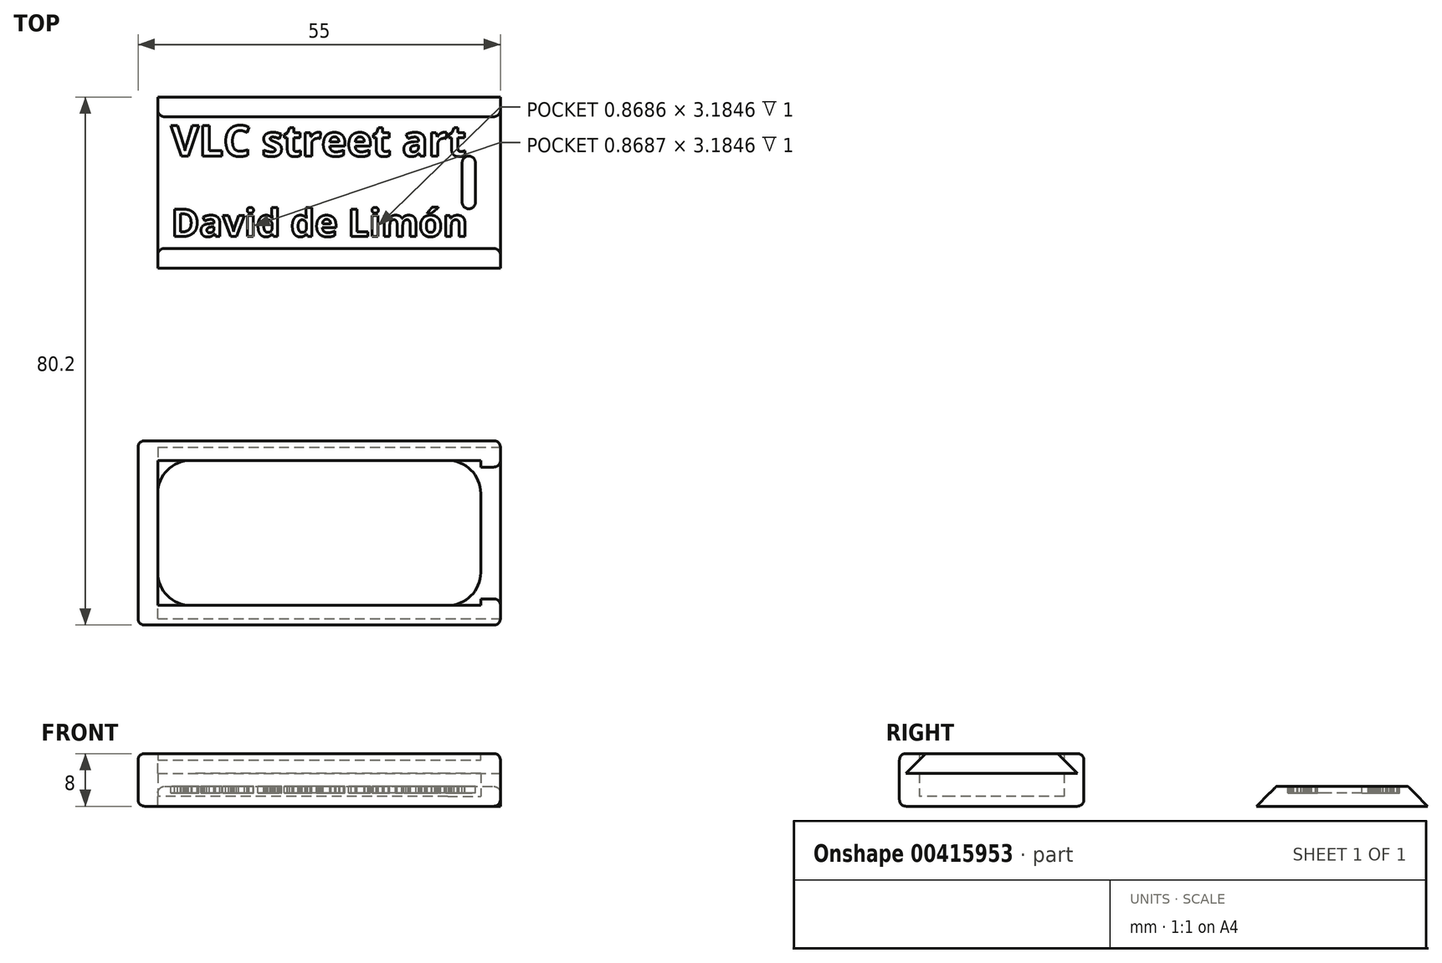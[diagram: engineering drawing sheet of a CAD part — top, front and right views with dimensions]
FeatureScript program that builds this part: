
annotation { "Feature Type Name" : "Feature", "Feature Type Description" : "" }
export const myFeature = defineFeature(function(context is Context, id is Id, definition is map)
    precondition{}
    {
        {
            assignVariable(context, id + "F0", {"name" : "Alto", "anyValue" : 2});
        }
        {
            assignVariable(context, id + "F1", {"name" : "largo", "anyValue" : 49});
        }
        {
            assignVariable(context, id + "F2", {"name" : "espesor", "anyValue" : 3});
        }
        {
            var Q0;
            Q0=qCreatedBy(makeId("Top.planeOp"),FACE);
            var sketch = newSketch(context, id + "F3", { "sketchPlane" : qUnion([Q0])});
            skLineSegment(sketch, "E0.bottom", {"start": v(24.5, 11) * mm, "end": v(-24.5, 11) * mm});
            skLineSegment(sketch, "E0.top", {"start": v(24.5, -11) * mm, "end": v(-24.5, -11) * mm});
            skLineSegment(sketch, "E0.left", {"start": v(24.5, 11) * mm, "end": v(24.5, -11) * mm});
            skLineSegment(sketch, "E0.right", {"start": v(-24.5, 11) * mm, "end": v(-24.5, -11) * mm});
            skPoint(sketch, "E0.middle", {"position": v(0, 0) * mm});
            skLineSegment(sketch, "E1.bottom", {"start": v(27.5, 14) * mm, "end": v(-27.5, 14) * mm});
            skLineSegment(sketch, "E1.top", {"start": v(27.5, -14) * mm, "end": v(-27.5, -14) * mm});
            skLineSegment(sketch, "E1.left", {"start": v(27.5, 14) * mm, "end": v(27.5, -14) * mm});
            skLineSegment(sketch, "E1.right", {"start": v(-27.5, 14) * mm, "end": v(-27.5, -14) * mm});
            skSolve(sketch);
        }
        {
            var Q0;
            Q0=makeQuery(id+"F3.imprint","IMPRINT",FACE,{"disambiguationData":[TD([[makeQuery(id+"F3.imprint","IMPRINT",EDGE,{"derivedFrom":sQuery(id+"F3.wireOp",EDGE,"E0.bottom")}),-1.0]])]});
            extrude(context, id + "F4", {"entities" : qUnion([Q0]), "depth" : (2 * getVariable(context, 'espesor') + getVariable(context, 'Alto')) * mm});
        }
        {
            var Q0;
            Q0=makeQuery(id+"F3.imprint","IMPRINT",FACE,{"disambiguationData":[TD([[makeQuery(id+"F3.imprint","IMPRINT",EDGE,{"derivedFrom":sQuery(id+"F3.wireOp",EDGE,"E0.bottom")}),1.0]])]});
            extrude(context, id + "F5", {"entities" : qUnion([Q0]), "operationType" : NewBodyOperationType.ADD, "depth" : (.5 * getVariable(context, 'espesor')) * mm});
        }
        {
            var Q0;
            Q0=makeQuery(id+"F4.opExtrude","SWEPT_FACE",FACE,{"disambiguationData":[OSD([sQuery(id+"F3.wireOp",EDGE,"E1.left")])]});
            var sketch = newSketch(context, id + "F6", { "sketchPlane" : qUnion([Q0])});
            skLineSegment(sketch, "E2", {"start": v(13, 5) * mm, "end": v(0, 5) * mm});
            skLineSegment(sketch, "E3", {"start": v(13, 5) * mm, "end": v(10, 8) * mm});
            skLineSegment(sketch, "E4", {"start": v(10, 8) * mm, "end": v(0, 8) * mm});
            skLineSegment(sketch, "E5.MirrorCS", {"start": v(-10, 8) * mm, "end": v(0, 8) * mm});
            skLineSegment(sketch, "E6.MirrorCS", {"start": v(-13, 5) * mm, "end": v(0, 5) * mm});
            skLineSegment(sketch, "E7.MirrorCS", {"start": v(-13, 5) * mm, "end": v(-10, 8) * mm});
            skSolve(sketch);
        }
        {
            var Q0;
            Q0=makeQuery(id+"F6.imprint","IMPRINT",FACE,{"disambiguationData":[TD([[makeQuery(id+"F6.imprint","IMPRINT",EDGE,{"derivedFrom":sQuery(id+"F6.wireOp",EDGE,"E2")}),-1.0]])]});
            extrude(context, id + "F7", {"entities" : qUnion([Q0]), "oppositeDirection" : true, "depth" : (getVariable(context, 'largo') + getVariable(context, 'espesor')) * mm});
        }
        {
            var Q0;
            Q0=makeQuery(id+"F7.opExtrude","SWEPT_BODY",BODY,{"disambiguationData":[OSD([sQuery(id+"F6.wireOp",EDGE,"SvTivXyg-bIk5-CTMK-920A-VDUx7YFhp4Xd"),sQuery(id+"F6.wireOp",EDGE,"NXYqkgHn-n5s3-E9hX-fx2y-YQDCVjQoqeno"),sQuery(id+"F6.wireOp",EDGE,"E2"),sQuery(id+"F6.wireOp",EDGE,"a3f9a05b-10ae-4f7d-80d1-88aed766babd0.MirrorCS"),sQuery(id+"F6.wireOp",EDGE,"1d98cbd7-637a-48a3-b701-6e80e332eecd0.MirrorCS"),sQuery(id+"F6.wireOp",EDGE,"f009dd86-6c0a-4020-9c2a-33f01825d16c0.MirrorCS")])]});
            transform(context, id + "F8", {"entities" : qUnion([Q0]), "transformType" : TransformType.TRANSLATION_3D, "dx" : 0 * mm, "dy" : 53.2 * mm, "dz" : 0 * mm, "makeCopy" : true});
        }
        {
            var Q0;
            Q0=makeQuery(id+"F4.opExtrude","SWEPT_EDGE",EDGE,{"disambiguationData":[OSD([sQuery(id+"F3.wireOp",EDGE,"E1.top"),sQuery(id+"F3.wireOp",EDGE,"E1.right")])]});
            var Q1;
            Q1=makeQuery(id+"F4.opExtrude","SWEPT_EDGE",EDGE,{"disambiguationData":[OSD([sQuery(id+"F3.wireOp",EDGE,"E1.bottom"),sQuery(id+"F3.wireOp",EDGE,"E1.right")])]});
            var Q2;
            Q2=makeQuery(id+"F4.opExtrude","SWEPT_EDGE",EDGE,{"disambiguationData":[OSD([sQuery(id+"F3.wireOp",EDGE,"E1.bottom"),sQuery(id+"F3.wireOp",EDGE,"E1.left")])]});
            var Q3;
            Q3=makeQuery(id+"F4.opExtrude","SWEPT_EDGE",EDGE,{"disambiguationData":[OSD([sQuery(id+"F3.wireOp",EDGE,"E1.top"),sQuery(id+"F3.wireOp",EDGE,"E1.left")])]});
            var Q4;
            Q4=makeQuery(id+"F4.opExtrude","CAP_EDGE",EDGE,{"disambiguationData":[OSD([sQuery(id+"F3.wireOp",EDGE,"E1.top")])],"isStart":false});
            var Q5;
            Q5=makeQuery(id+"F4.opExtrude","CAP_EDGE",EDGE,{"disambiguationData":[OSD([sQuery(id+"F3.wireOp",EDGE,"E1.bottom")])],"isStart":false});
            var Q6;
            Q6=makeQuery(id+"F4.opExtrude","CAP_EDGE",EDGE,{"disambiguationData":[OSD([sQuery(id+"F3.wireOp",EDGE,"E1.right")])],"isStart":false});
            var Q7;
            Q7=makeQuery(id+"F4.opExtrude","CAP_EDGE",EDGE,{"disambiguationData":[OSD([sQuery(id+"F3.wireOp",EDGE,"E1.top")])],"isStart":true});
            var Q8;
            Q8=makeQuery(id+"F4.opExtrude","CAP_EDGE",EDGE,{"disambiguationData":[OSD([sQuery(id+"F3.wireOp",EDGE,"E1.left")])],"isStart":true});
            var Q9;
            Q9=makeQuery(id+"F4.opExtrude","CAP_EDGE",EDGE,{"disambiguationData":[OSD([sQuery(id+"F3.wireOp",EDGE,"E1.bottom")])],"isStart":true});
            var Q10;
            Q10=makeQuery(id+"F4.opExtrude","CAP_EDGE",EDGE,{"disambiguationData":[OSD([sQuery(id+"F3.wireOp",EDGE,"E1.right")])],"isStart":true});
            var Q11;
            Q11=makeQuery(id+"F4.opExtrude","CAP_EDGE",EDGE,{"disambiguationData":[OSD([sQuery(id+"F3.wireOp",EDGE,"E1.left")])],"isStart":false});
            var Q12;
            Q12=makeQuery(id+"F8.opPattern","COPY",EDGE,{"derivedFrom":makeQuery(id+"F7.opExtrude","CAP_EDGE",EDGE,{"disambiguationData":[OSD([sQuery(id+"F6.wireOp",EDGE,"E4"),sQuery(id+"F6.wireOp",EDGE,"E5.MirrorCS")])],"isStart":false}),"instanceName":"1"});
            fillet(context, id + "F9", {"entities" : qUnion([Q0, Q1, Q2, Q3, Q4, Q5, Q6, Q7, Q8, Q9, Q10, Q11, Q12]), "radius" : 1 * mm, "tangentPropagation" : true, "allowEdgeOverflow" : false});
        }
        {
            var Q0;
            Q0=makeQuery(id+"F7.opExtrude","CAP_EDGE",EDGE,{"disambiguationData":[OSD([sQuery(id+"F6.wireOp",EDGE,"E4"),sQuery(id+"F6.wireOp",EDGE,"E5.MirrorCS")])],"isStart":true});
            var Q1;
            Q1=makeQuery(id+"F8.opPattern","COPY",EDGE,{"derivedFrom":makeQuery(id+"F7.opExtrude","CAP_EDGE",EDGE,{"disambiguationData":[OSD([sQuery(id+"F6.wireOp",EDGE,"E4"),sQuery(id+"F6.wireOp",EDGE,"E5.MirrorCS")])],"isStart":true}),"instanceName":"1"});
            fillet(context, id + "F10", {"entities" : qUnion([Q0, Q1]), "radius" : 1 * mm, "tangentPropagation" : true, "allowEdgeOverflow" : false});
        }
        {
            var Q0;
            Q0=makeQuery(id+"F7.opExtrude","SWEPT_BODY",BODY,{"disambiguationData":[OSD([sQuery(id+"F6.wireOp",EDGE,"E2"),sQuery(id+"F6.wireOp",EDGE,"E3"),sQuery(id+"F6.wireOp",EDGE,"E4"),sQuery(id+"F6.wireOp",EDGE,"E5.MirrorCS"),sQuery(id+"F6.wireOp",EDGE,"E6.MirrorCS"),sQuery(id+"F6.wireOp",EDGE,"E7.MirrorCS")])]});
            var Q1;
            Q1=makeQuery(id+"F4.opExtrude","SWEPT_BODY",BODY,{"disambiguationData":[OSD([sQuery(id+"F3.wireOp",EDGE,"E0.bottom"),sQuery(id+"F3.wireOp",EDGE,"E0.top"),sQuery(id+"F3.wireOp",EDGE,"E0.left"),sQuery(id+"F3.wireOp",EDGE,"E0.right"),sQuery(id+"F3.wireOp",EDGE,"E1.bottom"),sQuery(id+"F3.wireOp",EDGE,"E1.top"),sQuery(id+"F3.wireOp",EDGE,"E1.left"),sQuery(id+"F3.wireOp",EDGE,"E1.right")])]});
            booleanBodies(context, id + "F11", {"operationType" : BooleanOperationType.SUBTRACTION, "tools" : qUnion([Q0]), "targets" : qUnion([Q1])});
        }
        {
            var Q0;
            Q0=makeQuery(id+"F8.opPattern","COPY",FACE,{"derivedFrom":makeQuery(id+"F7.opExtrude","SWEPT_FACE",FACE,{"disambiguationData":[OSD([sQuery(id+"F6.wireOp",EDGE,"E4"),sQuery(id+"F6.wireOp",EDGE,"E5.MirrorCS")])]}),"instanceName":"1"});
            var sketch = newSketch(context, id + "F12", { "sketchPlane" : qUnion([Q0])});
            skText(sketch, "E8", { "text": "VLC street art", "fontName": "OpenSans-Bold.ttf"});
            skText(sketch, "E9", { "text": "David de Limón", "fontName": "OpenSans-Bold.ttf"});
            skLineSegment(sketch, "E10", {"start": v(-24.5, 53.2) * mm, "end": v(25.5, 53.2) * mm, "construction": true});
            skLineSegment(sketch, "E11", {"start": v(0, 35.02) * mm, "end": v(0, 65.75) * mm, "construction": true});
            skPoint(sketch, "E11.endSnap0", {"position": v(0, 59.55) * mm});
            skLineSegment(sketch, "E12.bottom", {"start": v(23.7, 56.2) * mm, "end": v(21.7, 56.2) * mm});
            skLineSegment(sketch, "E12.top", {"start": v(23.7, 50.2) * mm, "end": v(21.7, 50.2) * mm});
            skLineSegment(sketch, "E12.left", {"start": v(23.7, 56.2) * mm, "end": v(23.7, 50.2) * mm});
            skLineSegment(sketch, "E12.right", {"start": v(21.7, 56.2) * mm, "end": v(21.7, 50.2) * mm});
            skPoint(sketch, "E12.middle", {"position": v(22.7, 53.2) * mm});
            skArc(sketch, "E13", {"start": v(23.7, 56.2) * mm, "mid": v(22.7, 57.22) * mm, "end": v(21.7, 56.2) * mm});
            skArc(sketch, "E14", {"start": v(21.7, 50.2) * mm, "mid": v(22.7, 49.2) * mm, "end": v(23.7, 50.2) * mm});
            const initialGuessF12  = {"E8": [-0.0225, 0.0572, 1, 0, 0.0047], "E9": [-0.0225, 0.045, 1, 0, 0.0042]};
            skSetInitialGuess(sketch, initialGuessF12);
            skSolve(sketch);
        }
        {
            var Q0;
            Q0=qSketchRegion(id+"F12",true);
            extrude(context, id + "F13", {"entities" : qUnion([Q0]), "operationType" : NewBodyOperationType.REMOVE, "oppositeDirection" : true, "depth" : 1 * mm});
        }
        {
            var Q0;
            Q0=makeQuery(id+"F8.opPattern","COPY",BODY,{"derivedFrom":makeQuery(id+"F7.opExtrude","SWEPT_BODY",BODY,{"disambiguationData":[OSD([sQuery(id+"F6.wireOp",EDGE,"SvTivXyg-bIk5-CTMK-920A-VDUx7YFhp4Xd"),sQuery(id+"F6.wireOp",EDGE,"NXYqkgHn-n5s3-E9hX-fx2y-YQDCVjQoqeno"),sQuery(id+"F6.wireOp",EDGE,"E2"),sQuery(id+"F6.wireOp",EDGE,"a3f9a05b-10ae-4f7d-80d1-88aed766babd0.MirrorCS"),sQuery(id+"F6.wireOp",EDGE,"1d98cbd7-637a-48a3-b701-6e80e332eecd0.MirrorCS"),sQuery(id+"F6.wireOp",EDGE,"f009dd86-6c0a-4020-9c2a-33f01825d16c0.MirrorCS")])]}),"instanceName":"1"});
            transform(context, id + "F14", {"entities" : qUnion([Q0]), "transformType" : TransformType.TRANSLATION_3D, "dx" : 0 * mm, "dy" : 0 * mm, "dz" : -5 * mm, "makeCopy" : false});
        }
        {
            var Q0;
            {var subQ0=sQuery(id+"F6.wireOp",EDGE,"E6.MirrorCS");var subQ1=sQuery(id+"F6.wireOp",EDGE,"E2");var subQ2=sQuery(id+"F3.wireOp",EDGE,"E0.right");var subQ3=sQuery(id+"F3.wireOp",EDGE,"E0.top");Q0=makeQuery(id+"F11.opBoolean","SPLIT",EDGE,{"disambiguationData":[TD([makeQuery(id+"F7.opExtrude","SWEPT_FACE",FACE,{"disambiguationData":[OSD([subQ1,subQ0])]})])],"derivedFrom":makeQuery(id+"F4.opExtrude","SWEPT_EDGE",EDGE,{"disambiguationData":[OSD([subQ3,subQ2])]})});}
            var Q1;
            {var subQ0=sQuery(id+"F3.wireOp",EDGE,"E0.top");var subQ1=sQuery(id+"F3.wireOp",EDGE,"E0.left");Q1=makeQuery(id+"F11.opBoolean","SPLIT",EDGE,{"disambiguationData":[TD([makeQuery(id+"F7.opExtrude","SWEPT_FACE",FACE,{"disambiguationData":[OSD([sQuery(id+"F6.wireOp",EDGE,"E2"),sQuery(id+"F6.wireOp",EDGE,"E6.MirrorCS")])]})])],"derivedFrom":makeQuery(id+"F4.opExtrude","SWEPT_EDGE",EDGE,{"disambiguationData":[OSD([subQ0,subQ1])]})});}
            var Q2;
            {var subQ0=sQuery(id+"F3.wireOp",EDGE,"E0.bottom");var subQ1=sQuery(id+"F3.wireOp",EDGE,"E0.left");Q2=makeQuery(id+"F11.opBoolean","SPLIT",EDGE,{"disambiguationData":[TD([makeQuery(id+"F7.opExtrude","SWEPT_FACE",FACE,{"disambiguationData":[OSD([sQuery(id+"F6.wireOp",EDGE,"E2"),sQuery(id+"F6.wireOp",EDGE,"E6.MirrorCS")])]})])],"derivedFrom":makeQuery(id+"F4.opExtrude","SWEPT_EDGE",EDGE,{"disambiguationData":[OSD([subQ0,subQ1])]})});}
            var Q3;
            {var subQ0=sQuery(id+"F6.wireOp",EDGE,"E6.MirrorCS");var subQ1=sQuery(id+"F6.wireOp",EDGE,"E2");var subQ2=sQuery(id+"F3.wireOp",EDGE,"E0.right");var subQ3=sQuery(id+"F3.wireOp",EDGE,"E0.bottom");Q3=makeQuery(id+"F11.opBoolean","SPLIT",EDGE,{"disambiguationData":[TD([makeQuery(id+"F7.opExtrude","SWEPT_FACE",FACE,{"disambiguationData":[OSD([subQ1,subQ0])]})])],"derivedFrom":makeQuery(id+"F4.opExtrude","SWEPT_EDGE",EDGE,{"disambiguationData":[OSD([subQ3,subQ2])]})});}
            fillet(context, id + "F15", {"entities" : qUnion([Q0, Q1, Q2, Q3]), "radius" : 5 * mm, "tangentPropagation" : true, "allowEdgeOverflow" : false});
        }
    });
